# Revit family: 321321321
name_source: partatom
category: Furniture
revit_build: Autodesk Revit 2016 (Build: 20150220_1215(x64)
units: mm (PartAtom-declared; Revit-internal decimal feet)

## family parameters
Always vertical = Yes
Cut with Voids When Loaded = No
OmniClass Number = 23.40.20.00
OmniClass Title = General Furniture and Specialties
Room Calculation Point = No
Shared = No
Work Plane-Based = No

## types (13) — shared parameters
Arm Pad = okm_G721
Assembly Code = E2020200
Body = okm_G721
Casters = okm_G155
D = 600 mm
Frame = okm_silver FX4
H = 1080 mm  [stored 3.54331 ft]
Keynote = 12490
Kind = Chair
Leg = okm_silver FX4
Manufacturer = Okamura Corporation
Other = okm_G155
Product Categories = Office seating
URL = http://www.okamura.co.jp
W = 676 mm

## per-type parameters (varying)
| type | Back Mesh | Product Code/Color | Seat Mesh |
| FPG2(White) | okm_FSP2 | CC81BS_FPG2 | okm_FPA2 |
| FPG7(Beige) | okm_FSP7 | CC81BS_FPG7 | okm_FPA7 |
| FPG8(Dark Brown) | okm_FSP8 | CC81BS_FPG8 | okm_FPA8 |
| FPG3(Light Gray) | okm_FSR3 | CC81BS_FPG3 | okm_FPA3 |
| FPH2(Medium Gray) | okm_FSR2 | CC81BS_FPH2 | okm_FPB2 |
| FPG1(Balck) | okm_FSP1 | CC81BS_FPG1 | okm_FPA1 |
| FPG4(Dark Blue) | okm_FSR4 | CC81BS_FPG4 | okm_FPA4 |
| FPG6(Sage) | okm_FPA6 | CC81BS_FPG6 | okm_FTY6 |
| FPH5(Dark Green) | okm_FSR5 | CC81BS_FPH5 | okm_FPB5 |
| FPG5(Green) | okm_FTY5 | CC81BS_FPG5 | okm_FPA5 |
| FPH9(Yellow) | okm_FSR9 | CC81BS_FPH9 | okm_FPB9 |
| FPH8(Orange Red) | okm_FTY8 | CC81BS_FPH8 | okm_FPB8 |
| FPG9(Red) | okm_FSP9 | CC81BS_FPG9 | okm_FPA9 |

note: [stored X ft] marks values corroborated as IEEE doubles in the binary element streams (Revit-internal decimal feet)

## geometry (parser evidence)
native form markers: Sweep x3
no freeform markers — native parametric forms only
